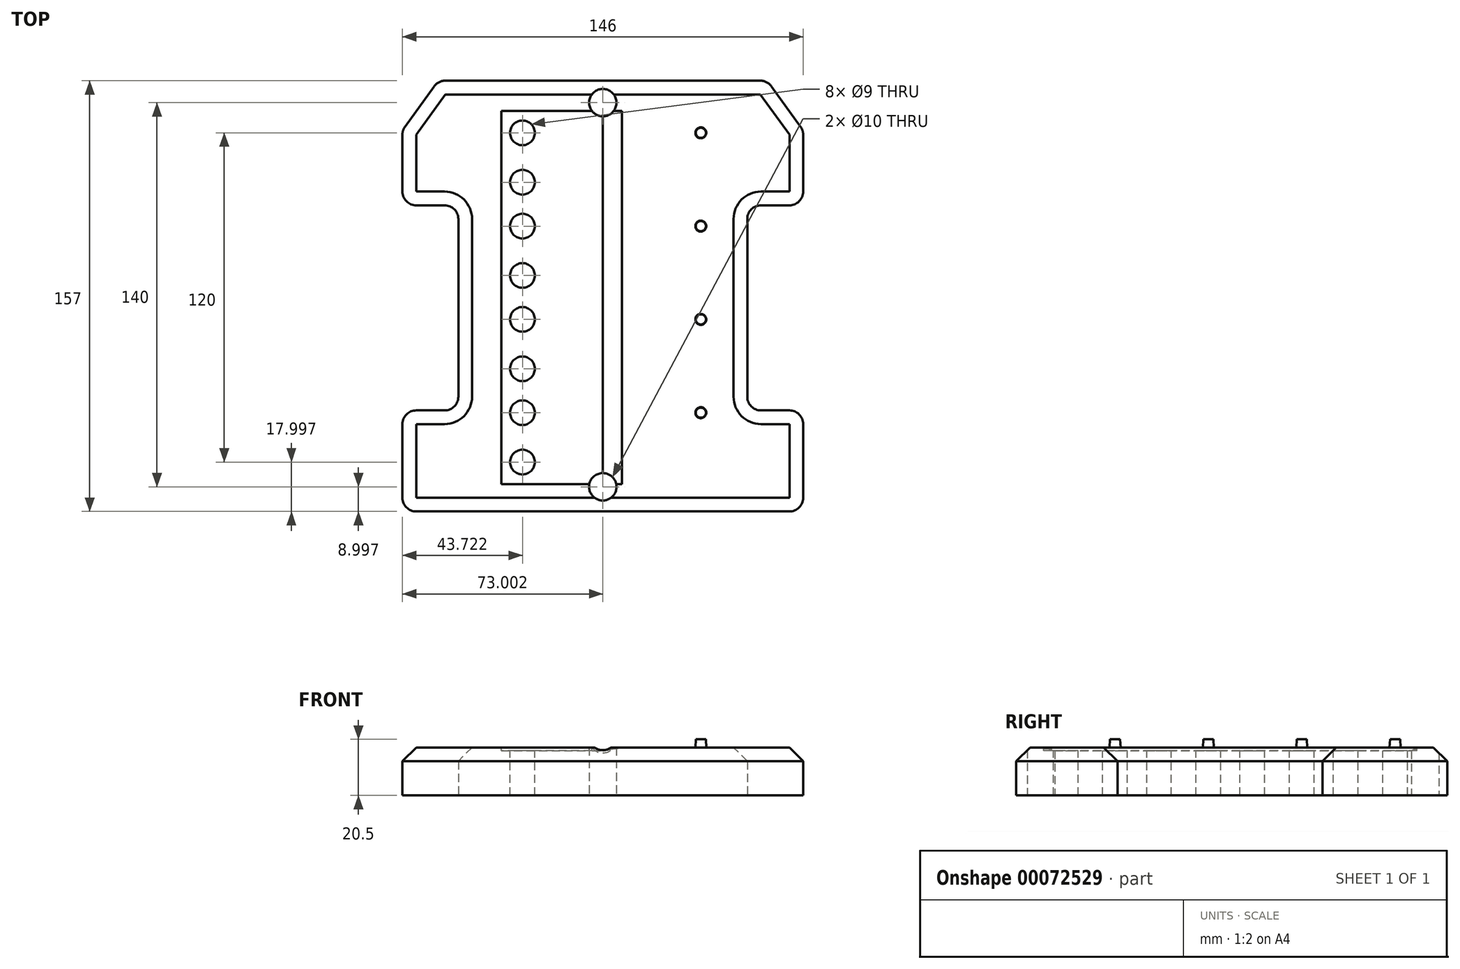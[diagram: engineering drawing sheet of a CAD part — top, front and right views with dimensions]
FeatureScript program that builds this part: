
annotation { "Feature Type Name" : "Feature", "Feature Type Description" : "" }
export const myFeature = defineFeature(function(context is Context, id is Id, definition is map)
    precondition{}
    {
        {
            var Q0;
            Q0=qCreatedBy(makeId("Top.planeOp"),FACE);
            var sketch = newSketch(context, id + "F0", { "sketchPlane" : qUnion([Q0])});
            skLineSegment(sketch, "E0.top", {"start": v(-75.98, -69.56) * mm, "end": v(70.02, -69.56) * mm});
            skLineSegment(sketch, "E0.left", {"start": v(-75.98, 69.44) * mm, "end": v(-75.98, 42.03) * mm});
            skLineSegment(sketch, "E0.right", {"start": v(70.02, 69.44) * mm, "end": v(70.02, 42.03) * mm});
            skCircle(sketch, "E1", {"center": v(-2.98, -60.56) * mm, "radius": 5 * mm});
            skPoint(sketch, "E1.centerSnap0", {"position": v(-2.98, -69.56) * mm});
            skCircle(sketch, "E2", {"center": v(-2.98, 79.44) * mm, "radius": 5 * mm});
            skPoint(sketch, "E2.centerSnap0", {"position": v(-2.98, 69.44) * mm});
            skLineSegment(sketch, "E3", {"start": v(-75.98, 69.44) * mm, "end": v(-62.98, 87.44) * mm});
            skLineSegment(sketch, "E4", {"start": v(-62.98, 87.44) * mm, "end": v(57.02, 87.44) * mm});
            skLineSegment(sketch, "E5", {"start": v(57.02, 87.44) * mm, "end": v(70.02, 69.44) * mm});
            skLineSegment(sketch, "E6", {"start": v(-2.98, 87.44) * mm, "end": v(-2.98, -69.56) * mm, "construction": true});
            skLineSegment(sketch, "E7", {"start": v(-75.98, 42.03) * mm, "end": v(-55.62, 42.03) * mm});
            skLineSegment(sketch, "E8", {"start": v(-55.62, 42.03) * mm, "end": v(-55.62, -32.72) * mm});
            skLineSegment(sketch, "E9", {"start": v(-55.62, -32.72) * mm, "end": v(-75.98, -32.72) * mm});
            skLineSegment(sketch, "E10.trimOffspring", {"start": v(-75.98, -32.72) * mm, "end": v(-75.98, -69.56) * mm});
            skLineSegment(sketch, "E11.MirrorCS", {"start": v(70.02, 42.03) * mm, "end": v(49.66, 42.03) * mm});
            skLineSegment(sketch, "E12.MirrorCS", {"start": v(49.66, 42.03) * mm, "end": v(49.66, -32.72) * mm});
            skLineSegment(sketch, "E13.MirrorCS", {"start": v(49.66, -32.72) * mm, "end": v(70.02, -32.72) * mm});
            skLineSegment(sketch, "E14.trimOffspring", {"start": v(70.02, -32.72) * mm, "end": v(70.02, -69.56) * mm});
            skSolve(sketch);
        }
        {
            var Q0;
            Q0=makeQuery(id+"F0.imprint","IMPRINT",FACE,{"disambiguationData":[TD([[makeQuery(id+"F0.imprint","IMPRINT",EDGE,{"derivedFrom":sQuery(id+"F0.wireOp",EDGE,"E0.top")}),1.0]])]});
            extrude(context, id + "F1", {"entities" : qUnion([Q0]), "depth" : 17.5 * mm});
        }
        {
            var Q0;
            Q0=makeQuery(id+"F1.opExtrude","CAP_FACE",FACE,{"disambiguationData":[OSD([sQuery(id+"F0.wireOp",EDGE,"E0.top"),sQuery(id+"F0.wireOp",EDGE,"E0.left"),sQuery(id+"F0.wireOp",EDGE,"E0.right"),sQuery(id+"F0.wireOp",EDGE,"E1"),sQuery(id+"F0.wireOp",EDGE,"E2"),sQuery(id+"F0.wireOp",EDGE,"E3"),sQuery(id+"F0.wireOp",EDGE,"E4"),sQuery(id+"F0.wireOp",EDGE,"E5")])],"isStart":false});
            var sketch = newSketch(context, id + "F2", { "sketchPlane" : qUnion([Q0])});
            skLineSegment(sketch, "E15.bottom", {"start": v(7.02, 76.44) * mm, "end": v(-39.98, 76.44) * mm});
            skLineSegment(sketch, "E15.left", {"start": v(7.02, 76.44) * mm, "end": v(7.02, -57.56) * mm});
            skLineSegment(sketch, "E15.right", {"start": v(-39.98, 76.44) * mm, "end": v(-39.98, -57.56) * mm});
            skCircle(sketch, "E16", {"center": v(-32.26, 68.44) * mm, "radius": 4.5 * mm});
            skCircle(sketch, "E17", {"center": v(-32.26, 50.44) * mm, "radius": 4.5 * mm});
            skCircle(sketch, "E18", {"center": v(-32.26, 34.44) * mm, "radius": 4.5 * mm});
            skCircle(sketch, "E19", {"center": v(-32.26, 16.44) * mm, "radius": 4.5 * mm});
            skCircle(sketch, "E20", {"center": v(-32.26, 0.44) * mm, "radius": 4.5 * mm});
            skCircle(sketch, "E21", {"center": v(-32.26, -17.56) * mm, "radius": 4.5 * mm});
            skCircle(sketch, "E22", {"center": v(-32.26, -33.56) * mm, "radius": 4.5 * mm});
            skCircle(sketch, "E23", {"center": v(-32.26, -51.56) * mm, "radius": 4.5 * mm});
            skCircle(sketch, "E24", {"center": v(32.74, 68.44) * mm, "radius": 2 * mm});
            skCircle(sketch, "E25", {"center": v(32.74, 34.44) * mm, "radius": 2 * mm});
            skCircle(sketch, "E26", {"center": v(32.74, 0.44) * mm, "radius": 2 * mm});
            skCircle(sketch, "E27", {"center": v(32.74, -33.56) * mm, "radius": 2 * mm});
            skLineSegment(sketch, "E28", {"start": v(-39.98, -57.56) * mm, "end": v(-39.98, -59.56) * mm});
            skLineSegment(sketch, "E29", {"start": v(-39.98, -59.56) * mm, "end": v(7.02, -59.56) * mm});
            skLineSegment(sketch, "E30", {"start": v(7.02, -57.56) * mm, "end": v(7.02, -59.56) * mm});
            skLineSegment(sketch, "E31", {"start": v(4.02, 76.44) * mm, "end": v(4.02, -59.56) * mm});
            skSolve(sketch);
        }
        {
            var Q0;
            Q0=makeQuery(id+"F2.imprint","IMPRINT",FACE,{"disambiguationData":[TD([[makeQuery(id+"F2.imprint","IMPRINT",EDGE,{"derivedFrom":sQuery(id+"F2.wireOp",EDGE,"E16")}),1.0]])]});
            var Q1;
            Q1=makeQuery(id+"F2.imprint","IMPRINT",FACE,{"disambiguationData":[TD([[makeQuery(id+"F2.imprint","IMPRINT",EDGE,{"derivedFrom":sQuery(id+"F2.wireOp",EDGE,"E17")}),1.0]])]});
            var Q2;
            Q2=makeQuery(id+"F2.imprint","IMPRINT",FACE,{"disambiguationData":[TD([[makeQuery(id+"F2.imprint","IMPRINT",EDGE,{"derivedFrom":sQuery(id+"F2.wireOp",EDGE,"E18")}),1.0]])]});
            var Q3;
            Q3=makeQuery(id+"F2.imprint","IMPRINT",FACE,{"disambiguationData":[TD([[makeQuery(id+"F2.imprint","IMPRINT",EDGE,{"derivedFrom":sQuery(id+"F2.wireOp",EDGE,"E19")}),1.0]])]});
            var Q4;
            Q4=makeQuery(id+"F2.imprint","IMPRINT",FACE,{"disambiguationData":[TD([[makeQuery(id+"F2.imprint","IMPRINT",EDGE,{"derivedFrom":sQuery(id+"F2.wireOp",EDGE,"E20")}),1.0]])]});
            var Q5;
            Q5=makeQuery(id+"F2.imprint","IMPRINT",FACE,{"disambiguationData":[TD([[makeQuery(id+"F2.imprint","IMPRINT",EDGE,{"derivedFrom":sQuery(id+"F2.wireOp",EDGE,"E21")}),1.0]])]});
            var Q6;
            Q6=makeQuery(id+"F2.imprint","IMPRINT",FACE,{"disambiguationData":[TD([[makeQuery(id+"F2.imprint","IMPRINT",EDGE,{"derivedFrom":sQuery(id+"F2.wireOp",EDGE,"E22")}),1.0]])]});
            var Q7;
            Q7=makeQuery(id+"F2.imprint","IMPRINT",FACE,{"disambiguationData":[TD([[makeQuery(id+"F2.imprint","IMPRINT",EDGE,{"derivedFrom":sQuery(id+"F2.wireOp",EDGE,"E23")}),1.0]])]});
            extrude(context, id + "F3", {"entities" : qUnion([Q0, Q1, Q2, Q3, Q4, Q5, Q6, Q7]), "operationType" : NewBodyOperationType.REMOVE, "endBound" : BoundingType.THROUGH_ALL, "oppositeDirection" : true, "depth" : 25 * mm});
        }
        {
            var Q0;
            {var subQ0=sQuery(id+"F2.wireOp",EDGE,"E15.right");Q0=makeQuery(id+"F2.imprint","IMPRINT",FACE,{"disambiguationData":[TD([[makeQuery(id+"F2.imprint","IMPRINT",EDGE,{"derivedFrom":subQ0}),1.0]])]});}
            extrude(context, id + "F4", {"entities" : qUnion([Q0]), "operationType" : NewBodyOperationType.REMOVE, "oppositeDirection" : true, "depth" : 1.25 * mm});
        }
        {
            var Q0;
            Q0=makeQuery(id+"F2.imprint","IMPRINT",FACE,{"disambiguationData":[TD([[makeQuery(id+"F2.imprint","IMPRINT",EDGE,{"derivedFrom":sQuery(id+"F2.wireOp",EDGE,"E24")}),1.0]])]});
            var Q1;
            Q1=makeQuery(id+"F2.imprint","IMPRINT",FACE,{"disambiguationData":[TD([[makeQuery(id+"F2.imprint","IMPRINT",EDGE,{"derivedFrom":sQuery(id+"F2.wireOp",EDGE,"E25")}),1.0]])]});
            var Q2;
            Q2=makeQuery(id+"F2.imprint","IMPRINT",FACE,{"disambiguationData":[TD([[makeQuery(id+"F2.imprint","IMPRINT",EDGE,{"derivedFrom":sQuery(id+"F2.wireOp",EDGE,"E26")}),1.0]])]});
            var Q3;
            Q3=makeQuery(id+"F2.imprint","IMPRINT",FACE,{"disambiguationData":[TD([[makeQuery(id+"F2.imprint","IMPRINT",EDGE,{"derivedFrom":sQuery(id+"F2.wireOp",EDGE,"E27")}),1.0]])]});
            extrude(context, id + "F5", {"entities" : qUnion([Q0, Q1, Q2, Q3]), "operationType" : NewBodyOperationType.ADD, "depth" : 3 * mm, "hasDraft" : true, "draftAngle" : 3 * degree, "draftPullDirection" : true});
        }
        {
            var Q0;
            Q0=makeQuery(id+"F1.opExtrude","SWEPT_EDGE",EDGE,{"disambiguationData":[OSD([sQuery(id+"F0.wireOp",EDGE,"E0.left"),sQuery(id+"F0.wireOp",EDGE,"E7")])]});
            var Q1;
            Q1=makeQuery(id+"F1.opExtrude","SWEPT_EDGE",EDGE,{"disambiguationData":[OSD([sQuery(id+"F0.wireOp",EDGE,"E0.right"),sQuery(id+"F0.wireOp",EDGE,"E11.MirrorCS")])]});
            var Q2;
            Q2=makeQuery(id+"F1.opExtrude","SWEPT_EDGE",EDGE,{"disambiguationData":[OSD([sQuery(id+"F0.wireOp",EDGE,"E0.right"),sQuery(id+"F0.wireOp",EDGE,"E5")])]});
            var Q3;
            Q3=makeQuery(id+"F1.opExtrude","SWEPT_EDGE",EDGE,{"disambiguationData":[OSD([sQuery(id+"F0.wireOp",EDGE,"E4"),sQuery(id+"F0.wireOp",EDGE,"E5")])]});
            var Q4;
            Q4=makeQuery(id+"F1.opExtrude","SWEPT_EDGE",EDGE,{"disambiguationData":[OSD([sQuery(id+"F0.wireOp",EDGE,"E3"),sQuery(id+"F0.wireOp",EDGE,"E4")])]});
            var Q5;
            Q5=makeQuery(id+"F1.opExtrude","SWEPT_EDGE",EDGE,{"disambiguationData":[OSD([sQuery(id+"F0.wireOp",EDGE,"E0.left"),sQuery(id+"F0.wireOp",EDGE,"E3")])]});
            var Q6;
            Q6=makeQuery(id+"F1.opExtrude","SWEPT_EDGE",EDGE,{"disambiguationData":[OSD([sQuery(id+"F0.wireOp",EDGE,"E7"),sQuery(id+"F0.wireOp",EDGE,"E8")])]});
            var Q7;
            Q7=makeQuery(id+"F1.opExtrude","SWEPT_EDGE",EDGE,{"disambiguationData":[OSD([sQuery(id+"F0.wireOp",EDGE,"E8"),sQuery(id+"F0.wireOp",EDGE,"E9")])]});
            var Q8;
            Q8=makeQuery(id+"F1.opExtrude","SWEPT_EDGE",EDGE,{"disambiguationData":[OSD([sQuery(id+"F0.wireOp",EDGE,"E9"),sQuery(id+"F0.wireOp",EDGE,"E10.trimOffspring")])]});
            var Q9;
            Q9=makeQuery(id+"F1.opExtrude","SWEPT_EDGE",EDGE,{"disambiguationData":[OSD([sQuery(id+"F0.wireOp",EDGE,"E0.top"),sQuery(id+"F0.wireOp",EDGE,"E10.trimOffspring")])]});
            var Q10;
            Q10=makeQuery(id+"F1.opExtrude","SWEPT_EDGE",EDGE,{"disambiguationData":[OSD([sQuery(id+"F0.wireOp",EDGE,"E0.top"),sQuery(id+"F0.wireOp",EDGE,"E14.trimOffspring")])]});
            var Q11;
            Q11=makeQuery(id+"F1.opExtrude","SWEPT_EDGE",EDGE,{"disambiguationData":[OSD([sQuery(id+"F0.wireOp",EDGE,"E13.MirrorCS"),sQuery(id+"F0.wireOp",EDGE,"E14.trimOffspring")])]});
            var Q12;
            Q12=makeQuery(id+"F1.opExtrude","SWEPT_EDGE",EDGE,{"disambiguationData":[OSD([sQuery(id+"F0.wireOp",EDGE,"E11.MirrorCS"),sQuery(id+"F0.wireOp",EDGE,"E12.MirrorCS")])]});
            var Q13;
            Q13=makeQuery(id+"F1.opExtrude","SWEPT_EDGE",EDGE,{"disambiguationData":[OSD([sQuery(id+"F0.wireOp",EDGE,"E12.MirrorCS"),sQuery(id+"F0.wireOp",EDGE,"E13.MirrorCS")])]});
            fillet(context, id + "F6", {"entities" : qUnion([Q0, Q1, Q2, Q3, Q4, Q5, Q6, Q7, Q8, Q9, Q10, Q11, Q12, Q13]), "radius" : 5 * mm, "tangentPropagation" : true, "allowEdgeOverflow" : false});
        }
        {
            var Q0;
            Q0=makeQuery(id+"F1.opExtrude","CAP_EDGE",EDGE,{"disambiguationData":[OSD([sQuery(id+"F0.wireOp",EDGE,"E4")])],"isStart":false});
            chamfer(context, id + "F7", {"entities" : qUnion([Q0]), "width" : 5 * mm, "tangentPropagation" : true});
        }
        {
            var Q0;
            Q0=qCreatedBy(makeId("Front.planeOp"),FACE);
            var Q1;
            Q1=sQuery(id+"F2.wireOp",EDGE,"E15.bottom");
            cPlane(context, id + "F8", {"entities" : qUnion([Q0, Q1]), "cplaneType" : CPlaneType.LINE_ANGLE, "offset" : 75 * mm, "angle" : 0 * degree, "width" : 150 * mm, "height" : 150 * mm});
        }
        {
            var Q0;
            Q0=qCreatedBy(id+"F8.planeOp",FACE);
            var sketch = newSketch(context, id + "F9", { "sketchPlane" : qUnion([Q0])});
            skLineSegment(sketch, "E32", {"start": v(-4.03, 17.5) * mm, "end": v(-4.03, 16.25) * mm});
            skLineSegment(sketch, "E33", {"start": v(-4.03, 16.25) * mm, "end": v(2.99, 16.25) * mm});
            skLineSegment(sketch, "E34", {"start": v(2.99, 16.25) * mm, "end": v(-4.03, 17.5) * mm});
            skSolve(sketch);
        }
        {
            var Q0;
            Q0=makeQuery(id+"F9.imprint","IMPRINT",FACE,{"disambiguationData":[TD([[makeQuery(id+"F9.imprint","IMPRINT",EDGE,{"derivedFrom":sQuery(id+"F9.wireOp",EDGE,"E32")}),1.0]])]});
            var Q1;
            {var subQ0=sQuery(id+"F2.wireOp",EDGE,"E29");Q1=makeQuery(id+"F4.boolean.opBoolean","COPY",FACE,{"derivedFrom":makeQuery(id+"F4.opExtrude","SWEPT_FACE",FACE,{"disambiguationData":[OSD([subQ0]),TDD([makeQuery(id+"F2.imprint","IMPRINT",EDGE,{"disambiguationData":[TD([[makeQuery(id+"F2.imprint","INTERSECT",VERTEX,{"derivedFrom":[subQ0,sQuery(id+"F2.wireOp",EDGE,"E31")]}),1.0]])],"derivedFrom":subQ0})])]})});}
            extrude(context, id + "F10", {"entities" : qUnion([Q0]), "operationType" : NewBodyOperationType.ADD, "endBound" : BoundingType.UP_TO_SURFACE, "oppositeDirection" : true, "endBoundEntityFace" : qUnion([Q1]), "depth" : 25 * mm});
        }
        {
            var Q0;
            Q0=makeQuery(id+"F0.imprint","IMPRINT",FACE,{"disambiguationData":[TD([[makeQuery(id+"F0.imprint","IMPRINT",EDGE,{"derivedFrom":sQuery(id+"F0.wireOp",EDGE,"E1")}),1.0]])]});
            var Q1;
            Q1=makeQuery(id+"F0.imprint","IMPRINT",FACE,{"disambiguationData":[TD([[makeQuery(id+"F0.imprint","IMPRINT",EDGE,{"derivedFrom":sQuery(id+"F0.wireOp",EDGE,"E2")}),1.0]])]});
            var Q2;
            Q2=makeQuery(id+"F7.opChamfer","SPLIT",FACE,{"disambiguationData":[OD(0.0)],"derivedFrom":makeQuery(id+"F1.opExtrude","CAP_FACE",FACE,{"disambiguationData":[OSD([sQuery(id+"F0.wireOp",EDGE,"E0.top"),sQuery(id+"F0.wireOp",EDGE,"E0.left"),sQuery(id+"F0.wireOp",EDGE,"E0.right"),sQuery(id+"F0.wireOp",EDGE,"E1"),sQuery(id+"F0.wireOp",EDGE,"E2"),sQuery(id+"F0.wireOp",EDGE,"E3"),sQuery(id+"F0.wireOp",EDGE,"E4"),sQuery(id+"F0.wireOp",EDGE,"E5"),sQuery(id+"F0.wireOp",EDGE,"E7"),sQuery(id+"F0.wireOp",EDGE,"E8"),sQuery(id+"F0.wireOp",EDGE,"E9"),sQuery(id+"F0.wireOp",EDGE,"E10.trimOffspring"),sQuery(id+"F0.wireOp",EDGE,"E11.MirrorCS"),sQuery(id+"F0.wireOp",EDGE,"E12.MirrorCS"),sQuery(id+"F0.wireOp",EDGE,"E13.MirrorCS"),sQuery(id+"F0.wireOp",EDGE,"E14.trimOffspring")])],"isStart":false})});
            extrude(context, id + "F11", {"entities" : qUnion([Q0, Q1]), "operationType" : NewBodyOperationType.REMOVE, "endBound" : BoundingType.UP_TO_SURFACE, "endBoundEntityFace" : qUnion([Q2]), "depth" : 25 * mm});
        }
    });
